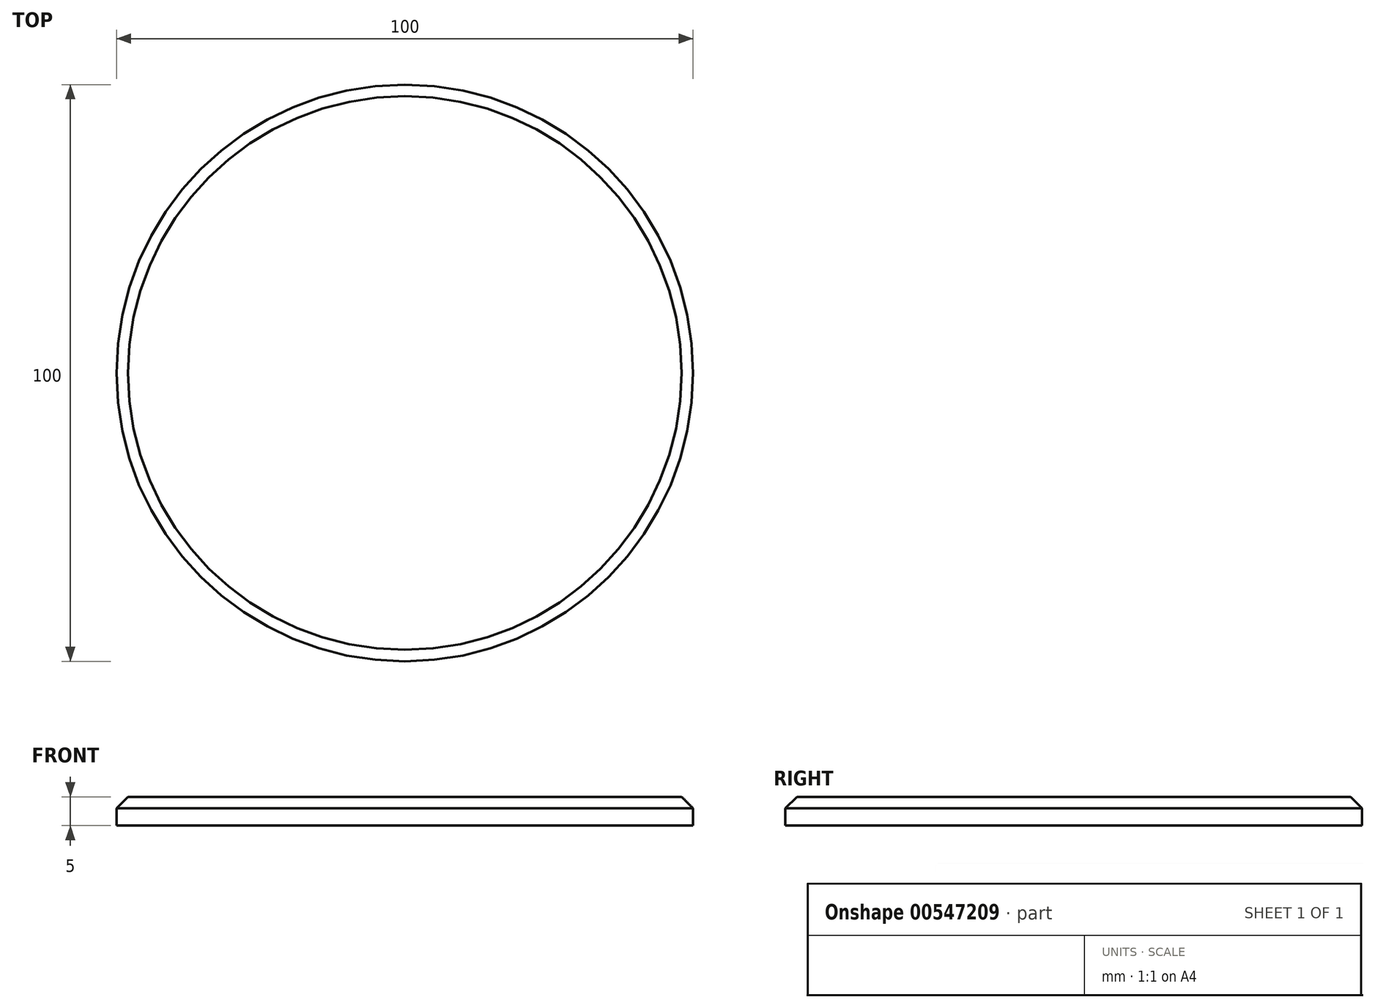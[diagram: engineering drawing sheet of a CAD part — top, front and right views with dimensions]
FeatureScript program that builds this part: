
annotation { "Feature Type Name" : "Feature", "Feature Type Description" : "" }
export const myFeature = defineFeature(function(context is Context, id is Id, definition is map)
    precondition{}
    {
        {
            var Q0;
            Q0=qCreatedBy(makeId("Top.planeOp"),FACE);
            var sketch = newSketch(context, id + "F0", { "sketchPlane" : qUnion([Q0])});
            skCircle(sketch, "E0", {"center": v(0, 0) * mm, "radius": 50 * mm});
            skSolve(sketch);
        }
        {
            var Q0;
            Q0 = qSketchRegion(id + "F0", true);
            extrude(context, id + "F1", {"entities" : qUnion([Q0]), "depth" : 5 * mm, "offsetDistance" : 25 * mm});
        }
        {
            var Q0;
            Q0=makeQuery(id+"F1.opExtrude","CAP_EDGE",EDGE,{"disambiguationData":[OSD([sQuery(id+"F0.wireOp",EDGE,"E0")])],"isStart":false});
            chamfer(context, id + "F2", {"entities" : qUnion([Q0]), "chamferType" : ChamferType.TWO_OFFSETS, "width1" : 2 * mm, "oppositeDirection" : false, "width2" : 2 * mm, "tangentPropagation" : true});
        }
    });
